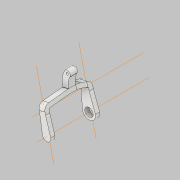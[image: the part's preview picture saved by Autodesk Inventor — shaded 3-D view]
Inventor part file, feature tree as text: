
AUTODESK INVENTOR PART (.ipt)
format: ipt  version: 2019.2 (Build 232265000, 265)  size: 583,680 bytes
history: native  units: mm
features: extrude x9, plane x9, sketch x8, other x7, fillet x3, chamfer x2, projected_geometry x2
ambient origin geometry x8: Origin, YZ Plane, XZ Plane, XY Plane, X Axis, Y Axis, Z Axis, Center Point
bodies: Volumenkörper1 (feature_tree)
feature tree (40):
  other  "LegBase.ipt"
  sketch  "Skizze2"  dims[d0=10.0mm d7=3.5mm d8=0.0mm]
  extrude  "Extrusion1"  Depth=3.5mm TaperAngle=0.0deg
  extrude  "Extrusion22"  Depth=1.5mm TaperAngle=0.0deg
  extrude  "Extrusion23"  Depth=4.5mm
  plane  "Arbeitsebene43"
  plane  "Arbeitsebene44"
  other  "Arbeitsachse8"
  other  "Arbeitspunkt8"
  extrude  "Extrusion50"  Depth=32.0mm
  other  "Arbeitsachse9"
  other  "Arbeitspunkt9"
  other  "Arbeitsachse10"
  plane  "Arbeitsebene57"
  sketch  "Skizze61"  dims[d251=11.5mm d261=7.0mm]
  extrude  "Extrusion51"  Depth=7.0mm
  extrude  "Extrusion52"  Depth=2.0mm
  extrude  "Extrusion53"  Depth=3.5mm
  chamfer  "Fase13"  Distance=1.0mm
  chamfer  "Fase14"  Distance=8.0mm
  other  "Arbeitsachse17"
  plane  "Arbeitsebene59"
  extrude  "Extrusion54"  Depth=5.0mm
  extrude  "Extrusion55"  Depth=2.0mm
  fillet  "Rundung37"  Radius=1.0mm
  fillet  "Rundung38"  Radius=3.0mm
  fillet  "Rundung39"  Radius=3.0mm
  sketch  "Skizze6"  dims[d100=2.0mm d136=1.5mm d137=0.0mm]
  sketch  "Skizze30"  dims[d138=3.0mm d139=0.0mm d158=4.5mm d200=10.0mm]
  plane  "Arbeitsebene45"
  plane  "Arbeitsebene46"
  sketch  "Skizze58"  dims[d230=11.0mm d237=32.0mm]
  plane  "Arbeitsebene47"
  plane  "Arbeitsebene48"
  sketch  "Skizze62"  dims[d262=5.0mm d263=2.0mm]
  projected_geometry  "Projizierte Kontur33"
  sketch  "Skizze63"  dims[d264=3.5mm d265=0.0mm d280=3.0mm]
  projected_geometry  "Projizierte Kontur34"
  plane  "Arbeitsebene58"
  sketch  "Skizze64"  dims[d281=6.0mm d282=1.0mm d283=8.0mm d284=5.0mm d285=3.0mm d286=1.0mm d287=3.0mm d288=0.0mm d289=3.0mm d290=0.0mm d291=3.0mm d292=0.0mm d293=1.0mm d294=8.0mm d295=45.0deg d296=1.0mm d297=8.0mm d298=45.0deg d301=2.1mm d302=3.490659mm d303=90.0deg d304=30.0mm d305=15.0mm d307=6.0mm d308=0.0mm d309=6.0mm d310=0.0mm d311=2.0mm d312=12.949388mm d313=0.25mm d314=0.25mm]
